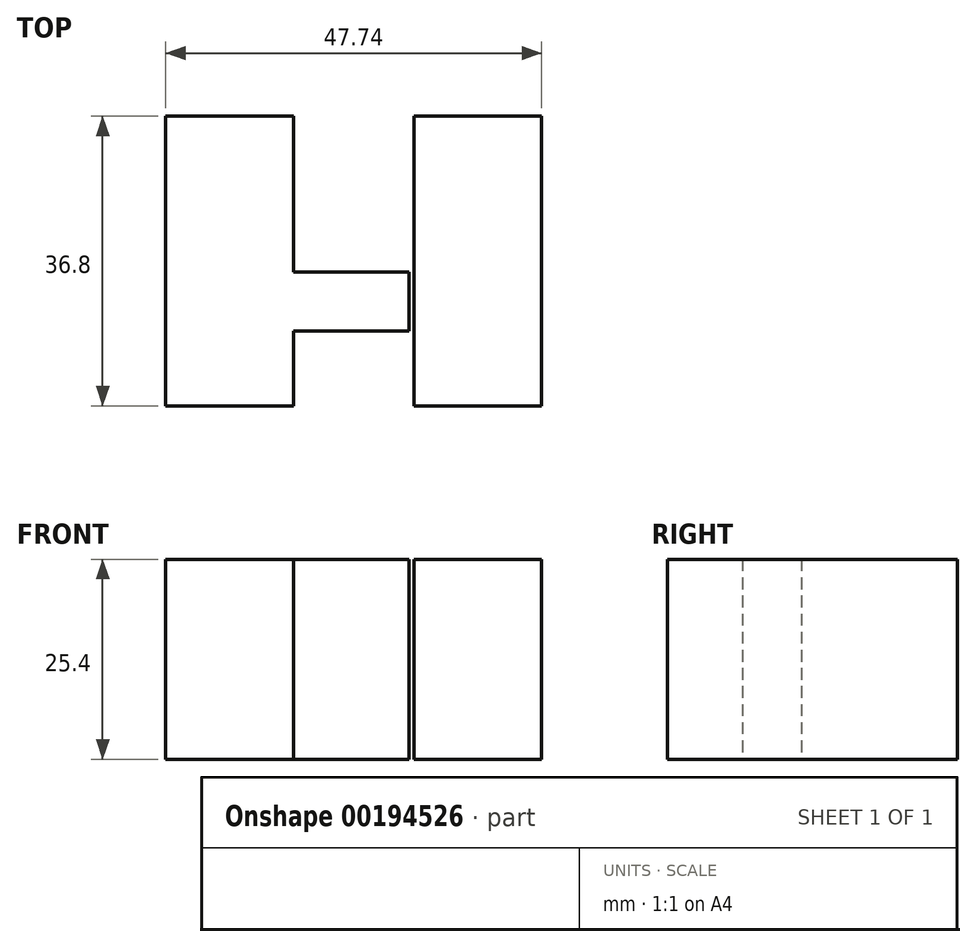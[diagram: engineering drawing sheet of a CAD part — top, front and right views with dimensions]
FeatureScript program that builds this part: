
annotation { "Feature Type Name" : "Feature", "Feature Type Description" : "" }
export const myFeature = defineFeature(function(context is Context, id is Id, definition is map)
    precondition{}
    {
        {
            var Q0;
            Q0=qCreatedBy(makeId("Top.planeOp"),FACE);
            var sketch = newSketch(context, id + "F0", { "sketchPlane" : qUnion([Q0])});
            skLineSegment(sketch, "E0.bottom", {"start": v(-36.5, 0) * mm, "end": v(-52.72, 0) * mm});
            skLineSegment(sketch, "E0.top", {"start": v(-36.5, 36.8) * mm, "end": v(-52.72, 36.8) * mm});
            skLineSegment(sketch, "E0.left", {"start": v(-36.5, 0) * mm, "end": v(-36.5, 36.8) * mm});
            skLineSegment(sketch, "E0.right", {"start": v(-52.72, 0) * mm, "end": v(-52.72, 36.8) * mm});
            skPoint(sketch, "E0.middle", {"position": v(-44.6, 18.4) * mm});
            skLineSegment(sketch, "E1.left", {"start": v(-36.5, 22) * mm, "end": v(-36.5, 12) * mm});
            skPoint(sketch, "E2.MirrorCS.end.orphan", {"position": v(24.02, 0) * mm});
            skPoint(sketch, "E2.MirrorCS.start.orphan", {"position": v(12.79, 0) * mm});
            skLineSegment(sketch, "E3.bottom", {"start": v(-36.5, 17) * mm, "end": v(-21.84, 17) * mm});
            skLineSegment(sketch, "E3.top", {"start": v(-36.5, 9.51) * mm, "end": v(-21.84, 9.51) * mm});
            skLineSegment(sketch, "E3.left", {"start": v(-36.5, 17) * mm, "end": v(-36.5, 9.51) * mm});
            skLineSegment(sketch, "E3.right", {"start": v(-21.84, 17) * mm, "end": v(-21.84, 9.51) * mm});
            skLineSegment(sketch, "E4.bottom", {"start": v(-4.98, 36.8) * mm, "end": v(-21.21, 36.8) * mm});
            skLineSegment(sketch, "E4.top", {"start": v(-4.98, 0) * mm, "end": v(-21.21, 0) * mm});
            skLineSegment(sketch, "E5", {"start": v(-21.21, 36.8) * mm, "end": v(-21.21, 0) * mm});
            skLineSegment(sketch, "E6", {"start": v(-4.98, 36.8) * mm, "end": v(-4.98, 0) * mm});
            skSolve(sketch);
        }
        {
            var Q0;
            {var subQ3=sQuery(id+"F0.wireOp",EDGE,"E3.bottom");Q0=makeQuery(id+"F0.imprint","IMPRINT",FACE,{"disambiguationData":[TD([[makeQuery(id+"F0.imprint","IMPRINT",EDGE,{"derivedFrom":subQ3}),-1.0]])]});}
            var Q1;
            Q1=makeQuery(id+"F0.imprint","IMPRINT",FACE,{"disambiguationData":[TD([[makeQuery(id+"F0.imprint","IMPRINT",EDGE,{"derivedFrom":sQuery(id+"F0.wireOp",EDGE,"E4.bottom")}),1.0]])]});
            var Q2;
            {var subQ3=sQuery(id+"F0.wireOp",EDGE,"E0.bottom");Q2=makeQuery(id+"F0.imprint","IMPRINT",FACE,{"disambiguationData":[TD([[makeQuery(id+"F0.imprint","IMPRINT",EDGE,{"derivedFrom":subQ3}),-1.0]])]});}
            extrude(context, id + "F1", {"entities" : qUnion([Q0, Q1, Q2]), "depth" : 25.4 * mm});
        }
    });
